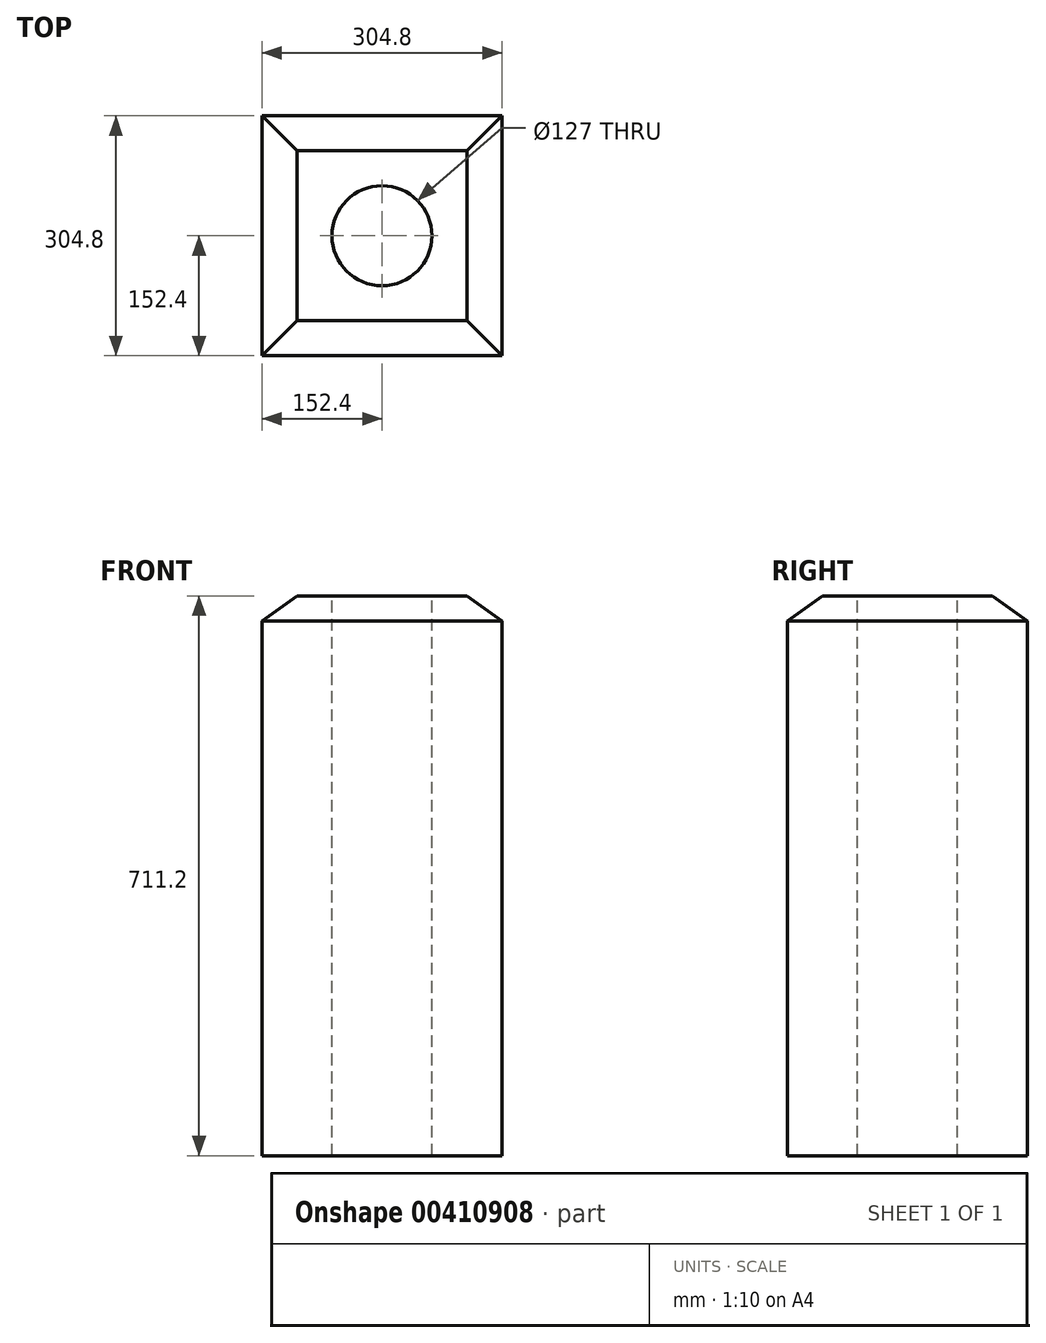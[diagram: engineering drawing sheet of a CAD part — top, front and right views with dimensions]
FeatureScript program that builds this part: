
annotation { "Feature Type Name" : "Feature", "Feature Type Description" : "" }
export const myFeature = defineFeature(function(context is Context, id is Id, definition is map)
    precondition{}
    {
        {
            var Q0;
            Q0=qCreatedBy(makeId("Top.planeOp"),FACE);
            var sketch = newSketch(context, id + "F0", { "sketchPlane" : qUnion([Q0])});
            skLineSegment(sketch, "E0", {"start": v(0, 0) * mm, "end": v(-304.8, 0) * mm});
            skLineSegment(sketch, "E1", {"start": v(-304.8, 0) * mm, "end": v(-304.8, 304.8) * mm});
            skLineSegment(sketch, "E2", {"start": v(-304.8, 304.8) * mm, "end": v(0, 304.8) * mm});
            skLineSegment(sketch, "E3", {"start": v(0, 304.8) * mm, "end": v(0, 0) * mm});
            skSolve(sketch);
        }
        {
            var Q0;
            Q0 = qSketchRegion(id + "F0", true);
            extrude(context, id + "F1", {"entities" : qUnion([Q0]), "depth" : 711.2 * mm});
        }
        {
            var Q0;
            Q0=makeQuery(id+"F1.opExtrude","CAP_EDGE",EDGE,{"disambiguationData":[OSD([sQuery(id+"F0.wireOp",EDGE,"E0")])],"isStart":false});
            var Q1;
            Q1=makeQuery(id+"F1.opExtrude","CAP_EDGE",EDGE,{"disambiguationData":[OSD([sQuery(id+"F0.wireOp",EDGE,"E3")])],"isStart":false});
            var Q2;
            Q2=makeQuery(id+"F1.opExtrude","CAP_EDGE",EDGE,{"disambiguationData":[OSD([sQuery(id+"F0.wireOp",EDGE,"E2")])],"isStart":false});
            var Q3;
            Q3=makeQuery(id+"F1.opExtrude","CAP_EDGE",EDGE,{"disambiguationData":[OSD([sQuery(id+"F0.wireOp",EDGE,"E1")])],"isStart":false});
            chamfer(context, id + "F2", {"entities" : qUnion([Q0, Q1, Q2, Q3]), "chamferType" : ChamferType.TWO_OFFSETS, "width1" : 31.75 * mm, "oppositeDirection" : false, "width2" : 44.45 * mm, "tangentPropagation" : true});
        }
        {
            var Q0;
            Q0=makeQuery(id+"F1.opExtrude","CAP_FACE",FACE,{"disambiguationData":[OSD([sQuery(id+"F0.wireOp",EDGE,"E0"),sQuery(id+"F0.wireOp",EDGE,"E1"),sQuery(id+"F0.wireOp",EDGE,"E2"),sQuery(id+"F0.wireOp",EDGE,"E3")])],"isStart":false});
            var sketch = newSketch(context, id + "F3", { "sketchPlane" : qUnion([Q0])});
            skLineSegment(sketch, "E4", {"start": v(-260.35, 260.35) * mm, "end": v(-44.45, 44.45) * mm});
            skCircle(sketch, "E5", {"center": v(-152.4, 152.4) * mm, "radius": 63.5 * mm});
            skSolve(sketch);
        }
        {
            var Q0;
            Q0 = qSketchRegion(id + "F3", true);
            extrude(context, id + "F4", {"entities" : qUnion([Q0]), "operationType" : NewBodyOperationType.REMOVE, "endBound" : BoundingType.THROUGH_ALL, "oppositeDirection" : true, "depth" : 25.4 * mm});
        }
    });
